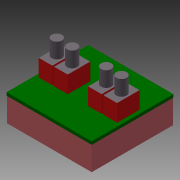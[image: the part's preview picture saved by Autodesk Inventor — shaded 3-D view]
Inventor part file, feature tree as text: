
AUTODESK INVENTOR PART (.ipt)
format: ipt  version: 2013 SP2 (Build 170200200, 200)  size: 174,080 bytes
history: native  units: mm
features: extrude x4, sketch x4, projected_geometry x3
ambient origin geometry x8: Origin, YZ Plane, XZ Plane, XY Plane, X Axis, Y Axis, Z Axis, Center Point
bodies: Solid1 (feature_tree)
feature tree (11):
  extrude  "Extrusion1"  Depth=48.0mm
  extrude  "Extrusion2"  Depth=8.0mm
  extrude  "Extrusion3"  Depth=24.5mm
  extrude  "Extrusion4"  Depth=8.0mm
  sketch  "Sketch1"  dims[d0=50.0mm d1=48.0mm]
  sketch  "Sketch4"  dims[d2=1.8mm d3=0.0mm d4=8.0mm]
  sketch  "Sketch5"  dims[d6=13.2mm d7=24.5mm]
  projected_geometry  "Projected Loop1"
  projected_geometry  "Projected Loop2"
  projected_geometry  "Projected Loop3"
  sketch  "Sketch6"  dims[d8=6.0mm d9=8.0mm d10=13.2mm d12=9.0mm d13=8.0mm d14=13.2mm d15=8.0mm d16=13.2mm d17=20.0mm d18=9.0mm d19=10.0mm d20=0.0mm d21=6.0mm d23=6.0mm d24=6.0mm d25=6.0mm d26=9.0mm d27=0.0mm d28=0.1mm d29=14.0mm d30=0.0mm]
